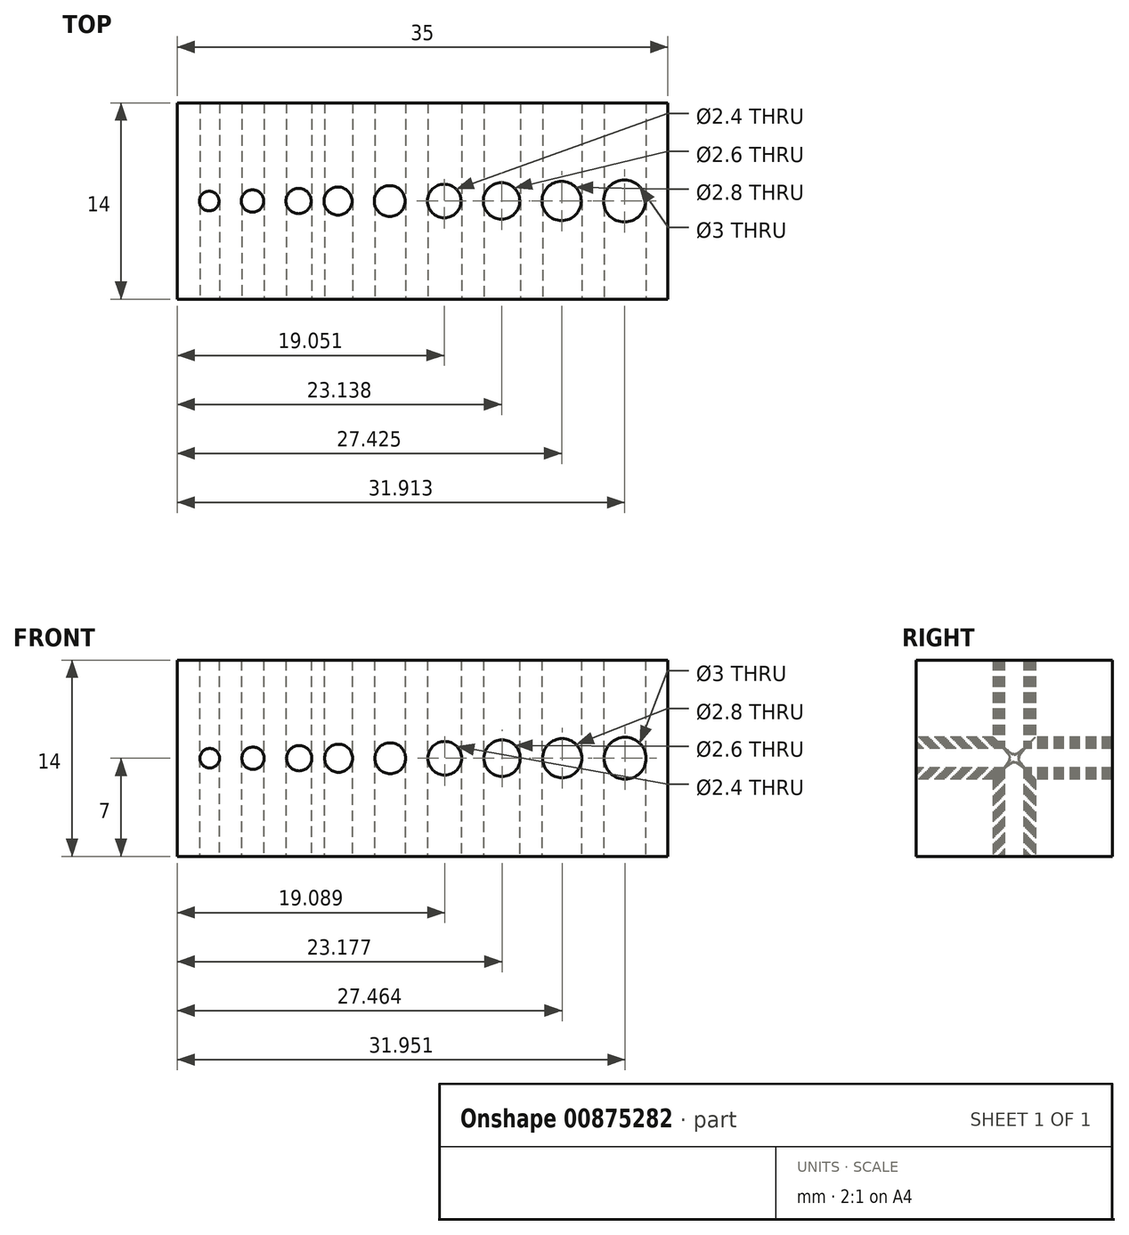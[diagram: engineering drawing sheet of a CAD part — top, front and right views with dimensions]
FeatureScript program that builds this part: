
annotation { "Feature Type Name" : "Feature", "Feature Type Description" : "" }
export const myFeature = defineFeature(function(context is Context, id is Id, definition is map)
    precondition{}
    {
        {
            var Q0;
            Q0=qCreatedBy(makeId("Top.planeOp"),FACE);
            var sketch = newSketch(context, id + "F0", { "sketchPlane" : qUnion([Q0])});
            skLineSegment(sketch, "E0.bottom", {"start": v(17.5, -7) * mm, "end": v(-17.5, -7) * mm});
            skLineSegment(sketch, "E0.top", {"start": v(17.5, 7) * mm, "end": v(-17.5, 7) * mm});
            skLineSegment(sketch, "E0.left", {"start": v(17.5, -7) * mm, "end": v(17.5, 7) * mm});
            skLineSegment(sketch, "E0.right", {"start": v(-17.5, -7) * mm, "end": v(-17.5, 7) * mm});
            skPoint(sketch, "E0.middle", {"position": v(0, 0) * mm});
            skCircle(sketch, "E1", {"center": v(-15.21, 0) * mm, "radius": 0.7 * mm});
            skCircle(sketch, "E2", {"center": v(-12.13, 0) * mm, "radius": 0.8 * mm});
            skCircle(sketch, "E3", {"center": v(-8.84, 0) * mm, "radius": 0.9 * mm});
            skCircle(sketch, "E4", {"center": v(-6.02, 0) * mm, "radius": 1 * mm});
            skCircle(sketch, "E5", {"center": v(-2.34, 0) * mm, "radius": 1.1 * mm});
            skCircle(sketch, "E6", {"center": v(1.55, 0) * mm, "radius": 1.2 * mm});
            skCircle(sketch, "E7", {"center": v(5.64, 0) * mm, "radius": 1.3 * mm});
            skCircle(sketch, "E8", {"center": v(9.93, 0) * mm, "radius": 1.4 * mm});
            skCircle(sketch, "E9", {"center": v(14.41, 0) * mm, "radius": 1.5 * mm});
            skLineSegment(sketch, "E10", {"start": v(-17.5, 0) * mm, "end": v(-15.91, 0) * mm, "construction": true});
            skLineSegment(sketch, "E11", {"start": v(-15.91, 0) * mm, "end": v(-14.51, 0) * mm, "construction": true});
            skLineSegment(sketch, "E12", {"start": v(-14.51, 0) * mm, "end": v(-12.93, 0) * mm, "construction": true});
            skLineSegment(sketch, "E13", {"start": v(-12.93, 0) * mm, "end": v(-11.33, 0) * mm, "construction": true});
            skLineSegment(sketch, "E14", {"start": v(-11.33, 0) * mm, "end": v(-9.74, 0) * mm, "construction": true});
            skLineSegment(sketch, "E15", {"start": v(-9.74, 0) * mm, "end": v(-7.94, 0) * mm, "construction": true});
            skLineSegment(sketch, "E16", {"start": v(-8.61, 0) * mm, "end": v(-7.94, 0) * mm, "construction": true});
            skLineSegment(sketch, "E17", {"start": v(-8.61, 0) * mm, "end": v(-7.02, 0) * mm, "construction": true});
            skLineSegment(sketch, "E18", {"start": v(-7.02, 0) * mm, "end": v(-5.02, 0) * mm, "construction": true});
            skLineSegment(sketch, "E19", {"start": v(-5.02, 0) * mm, "end": v(-3.44, 0) * mm, "construction": true});
            skLineSegment(sketch, "E20", {"start": v(-3.44, 0) * mm, "end": v(-1.24, 0) * mm, "construction": true});
            skLineSegment(sketch, "E21", {"start": v(-1.24, 0) * mm, "end": v(0.35, 0) * mm, "construction": true});
            skLineSegment(sketch, "E22", {"start": v(0.35, 0) * mm, "end": v(2.75, 0) * mm, "construction": true});
            skLineSegment(sketch, "E23", {"start": v(2.75, 0) * mm, "end": v(4.34, 0) * mm, "construction": true});
            skLineSegment(sketch, "E24", {"start": v(4.34, 0) * mm, "end": v(6.94, 0) * mm, "construction": true});
            skLineSegment(sketch, "E25", {"start": v(6.94, 0) * mm, "end": v(8.53, 0) * mm, "construction": true});
            skLineSegment(sketch, "E26", {"start": v(8.53, 0) * mm, "end": v(11.33, 0) * mm, "construction": true});
            skLineSegment(sketch, "E27", {"start": v(11.33, 0) * mm, "end": v(12.91, 0) * mm, "construction": true});
            skLineSegment(sketch, "E28", {"start": v(12.91, 0) * mm, "end": v(15.91, 0) * mm, "construction": true});
            skLineSegment(sketch, "E29", {"start": v(15.91, 0) * mm, "end": v(17.5, 0) * mm, "construction": true});
            skSolve(sketch);
        }
        {
            var Q0;
            Q0=makeQuery(id+"F0.imprint","IMPRINT",FACE,{"disambiguationData":[TD([[makeQuery(id+"F0.imprint","IMPRINT",EDGE,{"derivedFrom":sQuery(id+"F0.wireOp",EDGE,"E0.bottom")}),-1.0]])]});
            extrude(context, id + "F1", {"entities" : qUnion([Q0]), "depth" : 14 * mm, "offsetDistance" : 25 * mm});
        }
        {
            var Q0;
            Q0=makeQuery(id+"F1.opExtrude","SWEPT_FACE",FACE,{"disambiguationData":[OSD([sQuery(id+"F0.wireOp",EDGE,"E0.bottom")])]});
            var sketch = newSketch(context, id + "F2", { "sketchPlane" : qUnion([Q0])});
            skLineSegment(sketch, "E30.bottom", {"start": v(17.54, 0) * mm, "end": v(-17.46, 0) * mm});
            skLineSegment(sketch, "E30.top", {"start": v(17.54, 14) * mm, "end": v(-17.46, 14) * mm});
            skLineSegment(sketch, "E30.left", {"start": v(17.54, 0) * mm, "end": v(17.54, 14) * mm});
            skLineSegment(sketch, "E30.right", {"start": v(-17.46, 0) * mm, "end": v(-17.46, 14) * mm});
            skPoint(sketch, "E30.middle", {"position": v(0.04, 7) * mm});
            skCircle(sketch, "E31", {"center": v(-15.17, 7) * mm, "radius": 0.7 * mm});
            skCircle(sketch, "E32", {"center": v(-12.09, 7) * mm, "radius": 0.8 * mm});
            skCircle(sketch, "E33", {"center": v(-8.8, 7) * mm, "radius": 0.9 * mm});
            skCircle(sketch, "E34", {"center": v(-5.99, 7) * mm, "radius": 1 * mm});
            skCircle(sketch, "E35", {"center": v(-2.3, 7) * mm, "radius": 1.1 * mm});
            skCircle(sketch, "E36", {"center": v(1.59, 7) * mm, "radius": 1.2 * mm});
            skCircle(sketch, "E37", {"center": v(5.68, 7) * mm, "radius": 1.3 * mm});
            skCircle(sketch, "E38", {"center": v(9.96, 7) * mm, "radius": 1.4 * mm});
            skCircle(sketch, "E39", {"center": v(14.45, 7) * mm, "radius": 1.5 * mm});
            skLineSegment(sketch, "E40", {"start": v(-17.46, 7) * mm, "end": v(-15.87, 7) * mm, "construction": true});
            skLineSegment(sketch, "E41", {"start": v(-15.87, 7) * mm, "end": v(-14.47, 7) * mm, "construction": true});
            skLineSegment(sketch, "E42", {"start": v(-14.47, 7) * mm, "end": v(-12.89, 7) * mm, "construction": true});
            skLineSegment(sketch, "E43", {"start": v(-12.89, 7) * mm, "end": v(-11.29, 7) * mm, "construction": true});
            skLineSegment(sketch, "E44", {"start": v(-11.29, 7) * mm, "end": v(-9.7, 7) * mm, "construction": true});
            skLineSegment(sketch, "E45", {"start": v(-9.7, 7) * mm, "end": v(-7.9, 7) * mm, "construction": true});
            skLineSegment(sketch, "E46", {"start": v(-8.57, 7) * mm, "end": v(-7.9, 7) * mm, "construction": true});
            skLineSegment(sketch, "E47", {"start": v(-8.57, 7) * mm, "end": v(-6.99, 7) * mm, "construction": true});
            skLineSegment(sketch, "E48", {"start": v(-6.99, 7) * mm, "end": v(-4.99, 7) * mm, "construction": true});
            skLineSegment(sketch, "E49", {"start": v(-4.99, 7) * mm, "end": v(-3.4, 7) * mm, "construction": true});
            skLineSegment(sketch, "E50", {"start": v(-3.4, 7) * mm, "end": v(-1.2, 7) * mm, "construction": true});
            skLineSegment(sketch, "E51", {"start": v(-1.2, 7) * mm, "end": v(0.39, 7) * mm, "construction": true});
            skLineSegment(sketch, "E52", {"start": v(0.39, 7) * mm, "end": v(2.79, 7) * mm, "construction": true});
            skLineSegment(sketch, "E53", {"start": v(2.79, 7) * mm, "end": v(4.38, 7) * mm, "construction": true});
            skLineSegment(sketch, "E54", {"start": v(4.38, 7) * mm, "end": v(6.98, 7) * mm, "construction": true});
            skLineSegment(sketch, "E55", {"start": v(6.98, 7) * mm, "end": v(8.56, 7) * mm, "construction": true});
            skLineSegment(sketch, "E56", {"start": v(8.56, 7) * mm, "end": v(11.36, 7) * mm, "construction": true});
            skLineSegment(sketch, "E57", {"start": v(11.36, 7) * mm, "end": v(12.95, 7) * mm, "construction": true});
            skLineSegment(sketch, "E58", {"start": v(12.95, 7) * mm, "end": v(15.95, 7) * mm, "construction": true});
            skLineSegment(sketch, "E59", {"start": v(15.95, 7) * mm, "end": v(17.54, 7) * mm, "construction": true});
            skSolve(sketch);
        }
        {
            var Q0;
            Q0=makeQuery(id+"F2.imprint","IMPRINT",FACE,{"disambiguationData":[TD([[makeQuery(id+"F2.imprint","IMPRINT",EDGE,{"derivedFrom":sQuery(id+"F2.wireOp",EDGE,"E31")}),1.0]])]});
            var Q1;
            Q1=makeQuery(id+"F2.imprint","IMPRINT",FACE,{"disambiguationData":[TD([[makeQuery(id+"F2.imprint","IMPRINT",EDGE,{"derivedFrom":sQuery(id+"F2.wireOp",EDGE,"E32")}),1.0]])]});
            var Q2;
            Q2=makeQuery(id+"F2.imprint","IMPRINT",FACE,{"disambiguationData":[TD([[makeQuery(id+"F2.imprint","IMPRINT",EDGE,{"derivedFrom":sQuery(id+"F2.wireOp",EDGE,"E33")}),1.0]])]});
            var Q3;
            Q3=makeQuery(id+"F2.imprint","IMPRINT",FACE,{"disambiguationData":[TD([[makeQuery(id+"F2.imprint","IMPRINT",EDGE,{"derivedFrom":sQuery(id+"F2.wireOp",EDGE,"E34")}),1.0]])]});
            var Q4;
            Q4=makeQuery(id+"F2.imprint","IMPRINT",FACE,{"disambiguationData":[TD([[makeQuery(id+"F2.imprint","IMPRINT",EDGE,{"derivedFrom":sQuery(id+"F2.wireOp",EDGE,"E35")}),1.0]])]});
            var Q5;
            Q5=makeQuery(id+"F2.imprint","IMPRINT",FACE,{"disambiguationData":[TD([[makeQuery(id+"F2.imprint","IMPRINT",EDGE,{"derivedFrom":sQuery(id+"F2.wireOp",EDGE,"E36")}),1.0]])]});
            var Q6;
            Q6=makeQuery(id+"F2.imprint","IMPRINT",FACE,{"disambiguationData":[TD([[makeQuery(id+"F2.imprint","IMPRINT",EDGE,{"derivedFrom":sQuery(id+"F2.wireOp",EDGE,"E37")}),1.0]])]});
            var Q7;
            Q7=makeQuery(id+"F2.imprint","IMPRINT",FACE,{"disambiguationData":[TD([[makeQuery(id+"F2.imprint","IMPRINT",EDGE,{"derivedFrom":sQuery(id+"F2.wireOp",EDGE,"E38")}),1.0]])]});
            var Q8;
            Q8=makeQuery(id+"F2.imprint","IMPRINT",FACE,{"disambiguationData":[TD([[makeQuery(id+"F2.imprint","IMPRINT",EDGE,{"derivedFrom":sQuery(id+"F2.wireOp",EDGE,"E39")}),1.0]])]});
            var Q9;
            Q9=makeQuery(id+"F1.opExtrude","SWEPT_FACE",FACE,{"disambiguationData":[OSD([sQuery(id+"F0.wireOp",EDGE,"E0.top")])]});
            extrude(context, id + "F3", {"entities" : qUnion([Q0, Q1, Q2, Q3, Q4, Q5, Q6, Q7, Q8]), "operationType" : NewBodyOperationType.REMOVE, "endBound" : BoundingType.UP_TO_SURFACE, "oppositeDirection" : true, "depth" : 25 * mm, "endBoundEntityFace" : qUnion([Q9]), "offsetDistance" : 25 * mm});
        }
    });
